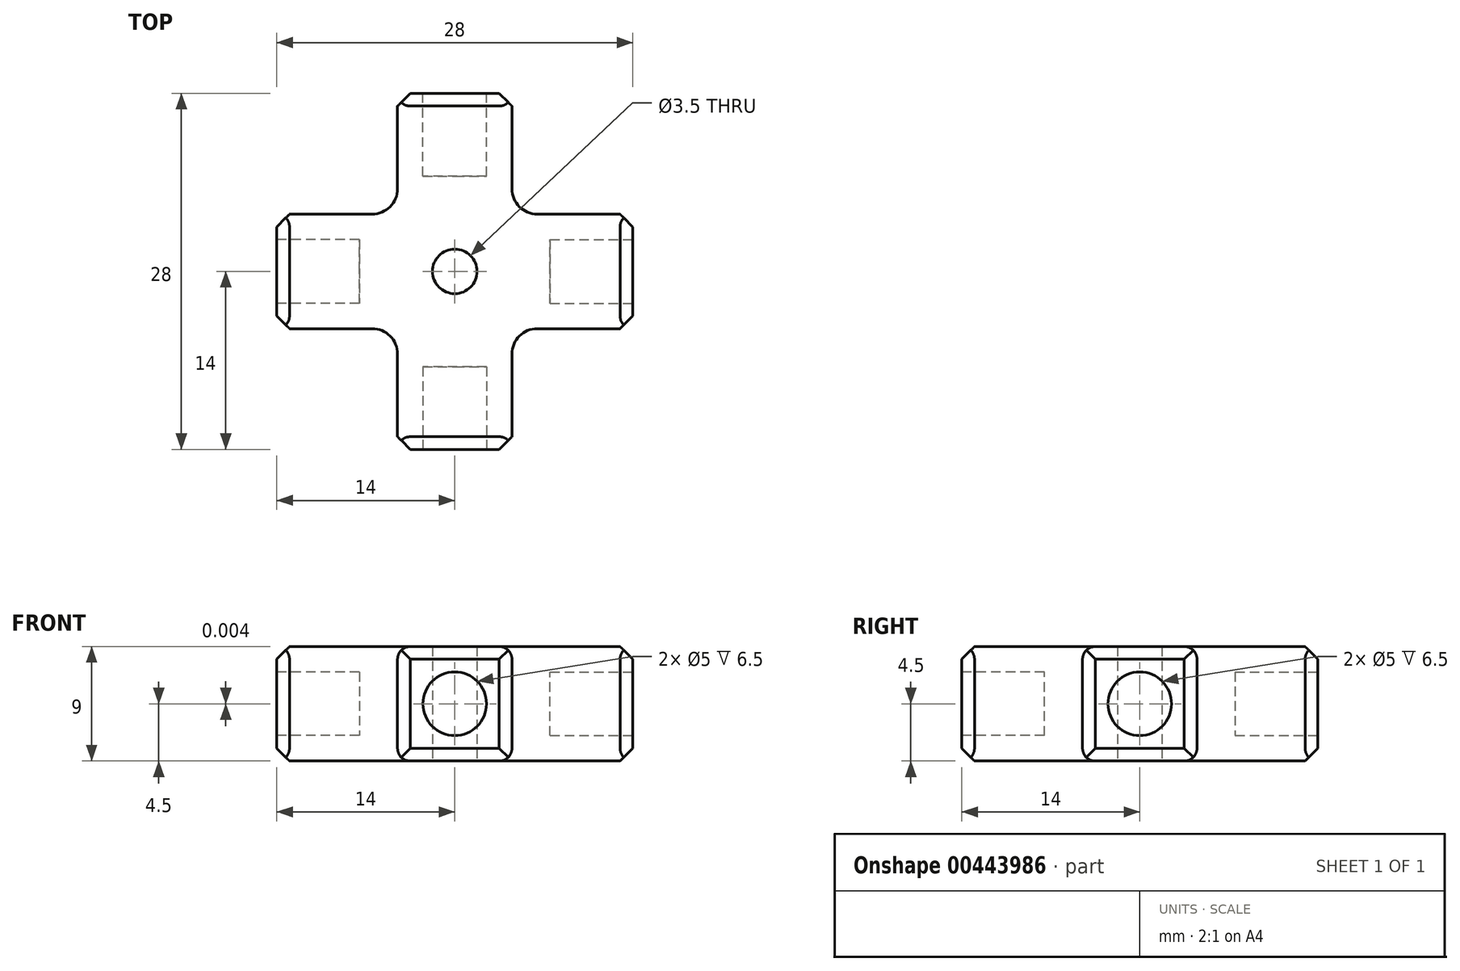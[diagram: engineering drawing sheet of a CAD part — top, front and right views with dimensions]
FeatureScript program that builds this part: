
annotation { "Feature Type Name" : "Feature", "Feature Type Description" : "" }
export const myFeature = defineFeature(function(context is Context, id is Id, definition is map)
    precondition{}
    {
        {
            var Q0;
            Q0=qCreatedBy(makeId("Top.planeOp"),FACE);
            var sketch = newSketch(context, id + "F0", { "sketchPlane" : qUnion([Q0])});
            skLineSegment(sketch, "E0.bottom", {"start": v(14, -14) * mm, "end": v(-14, -14) * mm});
            skLineSegment(sketch, "E0.top", {"start": v(14, 14) * mm, "end": v(-14, 14) * mm});
            skLineSegment(sketch, "E0.left", {"start": v(14, -14) * mm, "end": v(14, 14) * mm});
            skLineSegment(sketch, "E0.right", {"start": v(-14, -14) * mm, "end": v(-14, 14) * mm});
            skPoint(sketch, "E0.middle", {"position": v(0, 0) * mm});
            skLineSegment(sketch, "E1", {"start": v(-4.5, 14) * mm, "end": v(-4.5, -14) * mm});
            skLineSegment(sketch, "E2", {"start": v(4.5, 14) * mm, "end": v(4.5, -14) * mm});
            skLineSegment(sketch, "E3", {"start": v(-14, 4.5) * mm, "end": v(14, 4.5) * mm});
            skLineSegment(sketch, "E4", {"start": v(-14, -4.5) * mm, "end": v(14, -4.5) * mm});
            skCircle(sketch, "E5", {"center": v(0, 0) * mm, "radius": 1.75 * mm});
            skSolve(sketch);
        }
        {
            var Q0;
            {var subQ0=sQuery(id+"F0.wireOp",EDGE,"E1");var subQ1=sQuery(id+"F0.wireOp",EDGE,"E0.bottom");var subQ2=makeQuery(id+"F0.imprint","INTERSECT",VERTEX,{"derivedFrom":[subQ1,subQ0]});Q0=makeQuery(id+"F0.imprint","IMPRINT",FACE,{"disambiguationData":[TD([[makeQuery(id+"F0.imprint","IMPRINT",EDGE,{"disambiguationData":[TD([[subQ2,1.0]])],"derivedFrom":subQ1}),-1.0]])]});}
            var Q1;
            {var subQ0=sQuery(id+"F0.wireOp",EDGE,"E3");var subQ1=sQuery(id+"F0.wireOp",EDGE,"E0.left");var subQ2=makeQuery(id+"F0.imprint","INTERSECT",VERTEX,{"derivedFrom":[subQ1,subQ0]});Q1=makeQuery(id+"F0.imprint","IMPRINT",FACE,{"disambiguationData":[TD([[makeQuery(id+"F0.imprint","IMPRINT",EDGE,{"disambiguationData":[TD([[subQ2,1.0]])],"derivedFrom":subQ1}),1.0]])]});}
            var Q2;
            {var subQ0=sQuery(id+"F0.wireOp",EDGE,"E3");var subQ1=sQuery(id+"F0.wireOp",EDGE,"E0.right");var subQ2=makeQuery(id+"F0.imprint","INTERSECT",VERTEX,{"derivedFrom":[subQ1,subQ0]});Q2=makeQuery(id+"F0.imprint","IMPRINT",FACE,{"disambiguationData":[TD([[makeQuery(id+"F0.imprint","IMPRINT",EDGE,{"disambiguationData":[TD([[subQ2,1.0]])],"derivedFrom":subQ1}),-1.0]])]});}
            var Q3;
            {var subQ0=sQuery(id+"F0.wireOp",EDGE,"E1");var subQ1=sQuery(id+"F0.wireOp",EDGE,"E0.top");var subQ2=makeQuery(id+"F0.imprint","INTERSECT",VERTEX,{"derivedFrom":[subQ1,subQ0]});Q3=makeQuery(id+"F0.imprint","IMPRINT",FACE,{"disambiguationData":[TD([[makeQuery(id+"F0.imprint","IMPRINT",EDGE,{"disambiguationData":[TD([[subQ2,1.0]])],"derivedFrom":subQ1}),1.0]])]});}
            var Q4;
            {var subQ0=sQuery(id+"F0.wireOp",EDGE,"E3");var subQ1=sQuery(id+"F0.wireOp",EDGE,"E1");var subQ2=makeQuery(id+"F0.imprint","INTERSECT",VERTEX,{"derivedFrom":[subQ1,subQ0]});Q4=makeQuery(id+"F0.imprint","IMPRINT",FACE,{"disambiguationData":[TD([[makeQuery(id+"F0.imprint","IMPRINT",EDGE,{"disambiguationData":[TD([[subQ2,-1.0]])],"derivedFrom":subQ1}),1.0]])]});}
            extrude(context, id + "F1", {"entities" : qUnion([Q0, Q1, Q2, Q3, Q4]), "depth" : 9 * mm});
        }
        {
            var Q0;
            Q0=makeQuery(id+"F1.opExtrude","SWEPT_FACE",FACE,{"disambiguationData":[OSD([sQuery(id+"F0.wireOp",EDGE,"E0.top")])]});
            var sketch = newSketch(context, id + "F2", { "sketchPlane" : qUnion([Q0])});
            skLineSegment(sketch, "E6.0", {"start": v(-4.5, 0) * mm, "end": v(4.5, 0) * mm, "construction": true});
            skLineSegment(sketch, "E6.1", {"start": v(4.5, 9) * mm, "end": v(4.5, 0) * mm, "construction": true});
            skLineSegment(sketch, "E6.2", {"start": v(-4.5, 9) * mm, "end": v(4.5, 9) * mm, "construction": true});
            skLineSegment(sketch, "E6.3", {"start": v(-4.5, 9) * mm, "end": v(-4.5, 0) * mm, "construction": true});
            skLineSegment(sketch, "E7", {"start": v(0, 0) * mm, "end": v(0, 9) * mm, "construction": true});
            skLineSegment(sketch, "E8", {"start": v(4.5, 4.5) * mm, "end": v(-4.5, 4.5) * mm, "construction": true});
            skCircle(sketch, "E9", {"center": v(0, 4.5) * mm, "radius": 2.5 * mm});
            skSolve(sketch);
        }
        {
            var Q0;
            Q0=makeQuery(id+"F1.opExtrude","SWEPT_FACE",FACE,{"disambiguationData":[OSD([sQuery(id+"F0.wireOp",EDGE,"E0.left")])]});
            var sketch = newSketch(context, id + "F3", { "sketchPlane" : qUnion([Q0])});
            skLineSegment(sketch, "E10.0", {"start": v(-4.5, 9) * mm, "end": v(4.5, 9) * mm, "construction": true});
            skLineSegment(sketch, "E10.1", {"start": v(-4.5, 9) * mm, "end": v(-4.5, 0) * mm, "construction": true});
            skLineSegment(sketch, "E10.2", {"start": v(-4.5, 0) * mm, "end": v(4.5, 0) * mm, "construction": true});
            skLineSegment(sketch, "E10.3", {"start": v(4.5, 9) * mm, "end": v(4.5, 0) * mm, "construction": true});
            skLineSegment(sketch, "E11", {"start": v(0, 0) * mm, "end": v(0, 9) * mm, "construction": true});
            skLineSegment(sketch, "E12", {"start": v(-4.5, 4.5) * mm, "end": v(4.5, 4.5) * mm, "construction": true});
            skCircle(sketch, "E13", {"center": v(0, 4.5) * mm, "radius": 2.5 * mm});
            skSolve(sketch);
        }
        {
            var Q0;
            Q0=makeQuery(id+"F1.opExtrude","SWEPT_FACE",FACE,{"disambiguationData":[OSD([sQuery(id+"F0.wireOp",EDGE,"E0.right")])]});
            var sketch = newSketch(context, id + "F4", { "sketchPlane" : qUnion([Q0])});
            skLineSegment(sketch, "E14.0", {"start": v(4.5, 9) * mm, "end": v(-4.5, 9) * mm, "construction": true});
            skLineSegment(sketch, "E14.1", {"start": v(-4.5, 9) * mm, "end": v(-4.5, 0) * mm, "construction": true});
            skLineSegment(sketch, "E14.2", {"start": v(4.5, 0) * mm, "end": v(-4.5, 0) * mm, "construction": true});
            skLineSegment(sketch, "E14.3", {"start": v(4.5, 9) * mm, "end": v(4.5, 0) * mm, "construction": true});
            skCircle(sketch, "E15", {"center": v(0, 4.5) * mm, "radius": 2.5 * mm});
            skSolve(sketch);
        }
        {
            var Q0;
            Q0=makeQuery(id+"F1.opExtrude","SWEPT_FACE",FACE,{"disambiguationData":[OSD([sQuery(id+"F0.wireOp",EDGE,"E0.bottom")])]});
            var sketch = newSketch(context, id + "F5", { "sketchPlane" : qUnion([Q0])});
            skLineSegment(sketch, "E16.0", {"start": v(4.5, 9) * mm, "end": v(-4.5, 9) * mm, "construction": true});
            skLineSegment(sketch, "E16.1", {"start": v(-4.5, 9) * mm, "end": v(-4.5, 0) * mm, "construction": true});
            skLineSegment(sketch, "E16.2", {"start": v(4.5, 0) * mm, "end": v(-4.5, 0) * mm, "construction": true});
            skLineSegment(sketch, "E16.3", {"start": v(4.5, 9) * mm, "end": v(4.5, 0) * mm, "construction": true});
            skCircle(sketch, "E17", {"center": v(0, 4.5) * mm, "radius": 2.5 * mm});
            skSolve(sketch);
        }
        {
            var Q0;
            Q0=makeQuery(id+"F4.imprint","IMPRINT",FACE,{"disambiguationData":[TD([[makeQuery(id+"F4.imprint","IMPRINT",EDGE,{"derivedFrom":sQuery(id+"F4.wireOp",EDGE,"E15")}),1.0]])]});
            extrude(context, id + "F6", {"entities" : qUnion([Q0]), "operationType" : NewBodyOperationType.REMOVE, "oppositeDirection" : true, "depth" : 6.5 * mm});
        }
        {
            var Q0;
            Q0=makeQuery(id+"F3.imprint","IMPRINT",FACE,{"disambiguationData":[TD([[makeQuery(id+"F3.imprint","IMPRINT",EDGE,{"derivedFrom":sQuery(id+"F3.wireOp",EDGE,"E13")}),1.0]])]});
            extrude(context, id + "F7", {"entities" : qUnion([Q0]), "operationType" : NewBodyOperationType.REMOVE, "oppositeDirection" : true, "depth" : 6.5 * mm});
        }
        {
            var Q0;
            Q0=makeQuery(id+"F5.imprint","IMPRINT",FACE,{"disambiguationData":[TD([[makeQuery(id+"F5.imprint","IMPRINT",EDGE,{"derivedFrom":sQuery(id+"F5.wireOp",EDGE,"E17")}),1.0]])]});
            extrude(context, id + "F8", {"entities" : qUnion([Q0]), "operationType" : NewBodyOperationType.REMOVE, "oppositeDirection" : true, "depth" : 6.5 * mm});
        }
        {
            var Q0;
            Q0=makeQuery(id+"F2.imprint","IMPRINT",FACE,{"disambiguationData":[TD([[makeQuery(id+"F2.imprint","IMPRINT",EDGE,{"derivedFrom":sQuery(id+"F2.wireOp",EDGE,"E9")}),1.0]])]});
            extrude(context, id + "F9", {"entities" : qUnion([Q0]), "operationType" : NewBodyOperationType.REMOVE, "oppositeDirection" : true, "depth" : 6.5 * mm});
        }
        {
            var Q0;
            Q0=makeQuery(id+"F1.opExtrude","SWEPT_EDGE",EDGE,{"disambiguationData":[OSD([sQuery(id+"F0.wireOp",EDGE,"E1"),sQuery(id+"F0.wireOp",EDGE,"E3")])]});
            var Q1;
            Q1=makeQuery(id+"F1.opExtrude","SWEPT_EDGE",EDGE,{"disambiguationData":[OSD([sQuery(id+"F0.wireOp",EDGE,"E1"),sQuery(id+"F0.wireOp",EDGE,"E4")])]});
            var Q2;
            Q2=makeQuery(id+"F1.opExtrude","SWEPT_EDGE",EDGE,{"disambiguationData":[OSD([sQuery(id+"F0.wireOp",EDGE,"E2"),sQuery(id+"F0.wireOp",EDGE,"E4")])]});
            var Q3;
            Q3=makeQuery(id+"F1.opExtrude","SWEPT_EDGE",EDGE,{"disambiguationData":[OSD([sQuery(id+"F0.wireOp",EDGE,"E2"),sQuery(id+"F0.wireOp",EDGE,"E3")])]});
            fillet(context, id + "F10", {"entities" : qUnion([Q0, Q1, Q2, Q3]), "radius" : 2 * mm, "tangentPropagation" : true, "allowEdgeOverflow" : false});
        }
        {
            var Q0;
            Q0=makeQuery(id+"F1.opExtrude","SWEPT_EDGE",EDGE,{"disambiguationData":[OSD([sQuery(id+"F0.wireOp",EDGE,"E0.left"),sQuery(id+"F0.wireOp",EDGE,"E3")])]});
            var Q1;
            Q1=makeQuery(id+"F1.opExtrude","SWEPT_EDGE",EDGE,{"disambiguationData":[OSD([sQuery(id+"F0.wireOp",EDGE,"E0.top"),sQuery(id+"F0.wireOp",EDGE,"E2")])]});
            var Q2;
            Q2=makeQuery(id+"F1.opExtrude","SWEPT_EDGE",EDGE,{"disambiguationData":[OSD([sQuery(id+"F0.wireOp",EDGE,"E0.top"),sQuery(id+"F0.wireOp",EDGE,"E1")])]});
            var Q3;
            Q3=makeQuery(id+"F1.opExtrude","SWEPT_EDGE",EDGE,{"disambiguationData":[OSD([sQuery(id+"F0.wireOp",EDGE,"E0.right"),sQuery(id+"F0.wireOp",EDGE,"E3")])]});
            var Q4;
            Q4=makeQuery(id+"F1.opExtrude","SWEPT_EDGE",EDGE,{"disambiguationData":[OSD([sQuery(id+"F0.wireOp",EDGE,"E0.right"),sQuery(id+"F0.wireOp",EDGE,"E4")])]});
            var Q5;
            Q5=makeQuery(id+"F1.opExtrude","SWEPT_EDGE",EDGE,{"disambiguationData":[OSD([sQuery(id+"F0.wireOp",EDGE,"E0.bottom"),sQuery(id+"F0.wireOp",EDGE,"E1")])]});
            var Q6;
            Q6=makeQuery(id+"F1.opExtrude","SWEPT_EDGE",EDGE,{"disambiguationData":[OSD([sQuery(id+"F0.wireOp",EDGE,"E0.bottom"),sQuery(id+"F0.wireOp",EDGE,"E2")])]});
            var Q7;
            Q7=makeQuery(id+"F1.opExtrude","SWEPT_EDGE",EDGE,{"disambiguationData":[OSD([sQuery(id+"F0.wireOp",EDGE,"E0.left"),sQuery(id+"F0.wireOp",EDGE,"E4")])]});
            var Q8;
            Q8=makeQuery(id+"F1.opExtrude","CAP_EDGE",EDGE,{"disambiguationData":[OSD([sQuery(id+"F0.wireOp",EDGE,"E0.left")])],"isStart":true});
            var Q9;
            Q9=makeQuery(id+"F1.opExtrude","CAP_EDGE",EDGE,{"disambiguationData":[OSD([sQuery(id+"F0.wireOp",EDGE,"E0.top")])],"isStart":true});
            var Q10;
            Q10=makeQuery(id+"F1.opExtrude","CAP_EDGE",EDGE,{"disambiguationData":[OSD([sQuery(id+"F0.wireOp",EDGE,"E0.right")])],"isStart":true});
            var Q11;
            Q11=makeQuery(id+"F1.opExtrude","CAP_EDGE",EDGE,{"disambiguationData":[OSD([sQuery(id+"F0.wireOp",EDGE,"E0.bottom")])],"isStart":true});
            var Q12;
            Q12=makeQuery(id+"F1.opExtrude","CAP_EDGE",EDGE,{"disambiguationData":[OSD([sQuery(id+"F0.wireOp",EDGE,"E0.right")])],"isStart":false});
            var Q13;
            Q13=makeQuery(id+"F1.opExtrude","CAP_EDGE",EDGE,{"disambiguationData":[OSD([sQuery(id+"F0.wireOp",EDGE,"E0.top")])],"isStart":false});
            var Q14;
            Q14=makeQuery(id+"F1.opExtrude","CAP_EDGE",EDGE,{"disambiguationData":[OSD([sQuery(id+"F0.wireOp",EDGE,"E0.bottom")])],"isStart":false});
            var Q15;
            Q15=makeQuery(id+"F1.opExtrude","CAP_EDGE",EDGE,{"disambiguationData":[OSD([sQuery(id+"F0.wireOp",EDGE,"E0.left")])],"isStart":false});
            chamfer(context, id + "F11", {"entities" : qUnion([Q0, Q1, Q2, Q3, Q4, Q5, Q6, Q7, Q8, Q9, Q10, Q11, Q12, Q13, Q14, Q15]), "width" : 1 * mm, "tangentPropagation" : true});
        }
        {
            var Q0;
            {var subQ0=sQuery(id+"F0.wireOp",EDGE,"E4");Q0=makeQuery(id+"F1.opExtrude","CAP_EDGE",EDGE,{"disambiguationData":[OSD([subQ0]),TDD([makeQuery(id+"F0.imprint","IMPRINT",EDGE,{"disambiguationData":[TD([[makeQuery(id+"F0.imprint","INTERSECT",VERTEX,{"derivedFrom":[sQuery(id+"F0.wireOp",EDGE,"E0.right"),subQ0]}),-1.0]])],"derivedFrom":subQ0})])],"isStart":false});}
            var Q1;
            {var subQ0=sQuery(id+"F0.wireOp",EDGE,"E3");Q1=makeQuery(id+"F1.opExtrude","CAP_EDGE",EDGE,{"disambiguationData":[OSD([subQ0]),TDD([makeQuery(id+"F0.imprint","IMPRINT",EDGE,{"disambiguationData":[TD([[makeQuery(id+"F0.imprint","INTERSECT",VERTEX,{"derivedFrom":[sQuery(id+"F0.wireOp",EDGE,"E0.right"),subQ0]}),-1.0]])],"derivedFrom":subQ0})])],"isStart":false});}
            var Q2;
            {var subQ0=sQuery(id+"F0.wireOp",EDGE,"E1");Q2=makeQuery(id+"F1.opExtrude","CAP_EDGE",EDGE,{"disambiguationData":[OSD([subQ0]),TDD([makeQuery(id+"F0.imprint","IMPRINT",EDGE,{"disambiguationData":[TD([[makeQuery(id+"F0.imprint","INTERSECT",VERTEX,{"derivedFrom":[sQuery(id+"F0.wireOp",EDGE,"E0.bottom"),subQ0]}),1.0]])],"derivedFrom":subQ0})])],"isStart":false});}
            var Q3;
            {var subQ0=sQuery(id+"F0.wireOp",EDGE,"E2");Q3=makeQuery(id+"F1.opExtrude","CAP_EDGE",EDGE,{"disambiguationData":[OSD([subQ0]),TDD([makeQuery(id+"F0.imprint","IMPRINT",EDGE,{"disambiguationData":[TD([[makeQuery(id+"F0.imprint","INTERSECT",VERTEX,{"derivedFrom":[sQuery(id+"F0.wireOp",EDGE,"E0.bottom"),subQ0]}),1.0]])],"derivedFrom":subQ0})])],"isStart":false});}
            var Q4;
            {var subQ0=sQuery(id+"F0.wireOp",EDGE,"E4");Q4=makeQuery(id+"F1.opExtrude","CAP_EDGE",EDGE,{"disambiguationData":[OSD([subQ0]),TDD([makeQuery(id+"F0.imprint","IMPRINT",EDGE,{"disambiguationData":[TD([[makeQuery(id+"F0.imprint","INTERSECT",VERTEX,{"derivedFrom":[sQuery(id+"F0.wireOp",EDGE,"E0.left"),subQ0]}),1.0]])],"derivedFrom":subQ0})])],"isStart":false});}
            var Q5;
            {var subQ0=sQuery(id+"F0.wireOp",EDGE,"E3");Q5=makeQuery(id+"F1.opExtrude","CAP_EDGE",EDGE,{"disambiguationData":[OSD([subQ0]),TDD([makeQuery(id+"F0.imprint","IMPRINT",EDGE,{"disambiguationData":[TD([[makeQuery(id+"F0.imprint","INTERSECT",VERTEX,{"derivedFrom":[sQuery(id+"F0.wireOp",EDGE,"E0.left"),subQ0]}),1.0]])],"derivedFrom":subQ0})])],"isStart":false});}
            var Q6;
            {var subQ0=sQuery(id+"F0.wireOp",EDGE,"E2");Q6=makeQuery(id+"F1.opExtrude","CAP_EDGE",EDGE,{"disambiguationData":[OSD([subQ0]),TDD([makeQuery(id+"F0.imprint","IMPRINT",EDGE,{"disambiguationData":[TD([[makeQuery(id+"F0.imprint","INTERSECT",VERTEX,{"derivedFrom":[sQuery(id+"F0.wireOp",EDGE,"E0.top"),subQ0]}),-1.0]])],"derivedFrom":subQ0})])],"isStart":false});}
            var Q7;
            {var subQ0=sQuery(id+"F0.wireOp",EDGE,"E1");Q7=makeQuery(id+"F1.opExtrude","CAP_EDGE",EDGE,{"disambiguationData":[OSD([subQ0]),TDD([makeQuery(id+"F0.imprint","IMPRINT",EDGE,{"disambiguationData":[TD([[makeQuery(id+"F0.imprint","INTERSECT",VERTEX,{"derivedFrom":[sQuery(id+"F0.wireOp",EDGE,"E0.top"),subQ0]}),-1.0]])],"derivedFrom":subQ0})])],"isStart":false});}
            var Q8;
            {var subQ0=sQuery(id+"F0.wireOp",EDGE,"E3");Q8=makeQuery(id+"F1.opExtrude","CAP_EDGE",EDGE,{"disambiguationData":[OSD([subQ0]),TDD([makeQuery(id+"F0.imprint","IMPRINT",EDGE,{"disambiguationData":[TD([[makeQuery(id+"F0.imprint","INTERSECT",VERTEX,{"derivedFrom":[sQuery(id+"F0.wireOp",EDGE,"E0.right"),subQ0]}),-1.0]])],"derivedFrom":subQ0})])],"isStart":true});}
            var Q9;
            {var subQ0=sQuery(id+"F0.wireOp",EDGE,"E4");Q9=makeQuery(id+"F1.opExtrude","CAP_EDGE",EDGE,{"disambiguationData":[OSD([subQ0]),TDD([makeQuery(id+"F0.imprint","IMPRINT",EDGE,{"disambiguationData":[TD([[makeQuery(id+"F0.imprint","INTERSECT",VERTEX,{"derivedFrom":[sQuery(id+"F0.wireOp",EDGE,"E0.right"),subQ0]}),-1.0]])],"derivedFrom":subQ0})])],"isStart":true});}
            var Q10;
            {var subQ0=sQuery(id+"F0.wireOp",EDGE,"E1");Q10=makeQuery(id+"F1.opExtrude","CAP_EDGE",EDGE,{"disambiguationData":[OSD([subQ0]),TDD([makeQuery(id+"F0.imprint","IMPRINT",EDGE,{"disambiguationData":[TD([[makeQuery(id+"F0.imprint","INTERSECT",VERTEX,{"derivedFrom":[sQuery(id+"F0.wireOp",EDGE,"E0.bottom"),subQ0]}),1.0]])],"derivedFrom":subQ0})])],"isStart":true});}
            var Q11;
            {var subQ0=sQuery(id+"F0.wireOp",EDGE,"E2");Q11=makeQuery(id+"F1.opExtrude","CAP_EDGE",EDGE,{"disambiguationData":[OSD([subQ0]),TDD([makeQuery(id+"F0.imprint","IMPRINT",EDGE,{"disambiguationData":[TD([[makeQuery(id+"F0.imprint","INTERSECT",VERTEX,{"derivedFrom":[sQuery(id+"F0.wireOp",EDGE,"E0.bottom"),subQ0]}),1.0]])],"derivedFrom":subQ0})])],"isStart":true});}
            var Q12;
            {var subQ0=sQuery(id+"F0.wireOp",EDGE,"E4");Q12=makeQuery(id+"F1.opExtrude","CAP_EDGE",EDGE,{"disambiguationData":[OSD([subQ0]),TDD([makeQuery(id+"F0.imprint","IMPRINT",EDGE,{"disambiguationData":[TD([[makeQuery(id+"F0.imprint","INTERSECT",VERTEX,{"derivedFrom":[sQuery(id+"F0.wireOp",EDGE,"E0.left"),subQ0]}),1.0]])],"derivedFrom":subQ0})])],"isStart":true});}
            var Q13;
            {var subQ0=sQuery(id+"F0.wireOp",EDGE,"E3");Q13=makeQuery(id+"F1.opExtrude","CAP_EDGE",EDGE,{"disambiguationData":[OSD([subQ0]),TDD([makeQuery(id+"F0.imprint","IMPRINT",EDGE,{"disambiguationData":[TD([[makeQuery(id+"F0.imprint","INTERSECT",VERTEX,{"derivedFrom":[sQuery(id+"F0.wireOp",EDGE,"E0.left"),subQ0]}),1.0]])],"derivedFrom":subQ0})])],"isStart":true});}
            var Q14;
            {var subQ0=sQuery(id+"F0.wireOp",EDGE,"E2");Q14=makeQuery(id+"F1.opExtrude","CAP_EDGE",EDGE,{"disambiguationData":[OSD([subQ0]),TDD([makeQuery(id+"F0.imprint","IMPRINT",EDGE,{"disambiguationData":[TD([[makeQuery(id+"F0.imprint","INTERSECT",VERTEX,{"derivedFrom":[sQuery(id+"F0.wireOp",EDGE,"E0.top"),subQ0]}),-1.0]])],"derivedFrom":subQ0})])],"isStart":true});}
            var Q15;
            {var subQ0=sQuery(id+"F0.wireOp",EDGE,"E1");Q15=makeQuery(id+"F1.opExtrude","CAP_EDGE",EDGE,{"disambiguationData":[OSD([subQ0]),TDD([makeQuery(id+"F0.imprint","IMPRINT",EDGE,{"disambiguationData":[TD([[makeQuery(id+"F0.imprint","INTERSECT",VERTEX,{"derivedFrom":[sQuery(id+"F0.wireOp",EDGE,"E0.top"),subQ0]}),-1.0]])],"derivedFrom":subQ0})])],"isStart":true});}
            fillet(context, id + "F12", {"entities" : qUnion([Q0, Q1, Q2, Q3, Q4, Q5, Q6, Q7, Q8, Q9, Q10, Q11, Q12, Q13, Q14, Q15]), "radius" : 1 * mm, "tangentPropagation" : true, "allowEdgeOverflow" : false});
        }
    });
